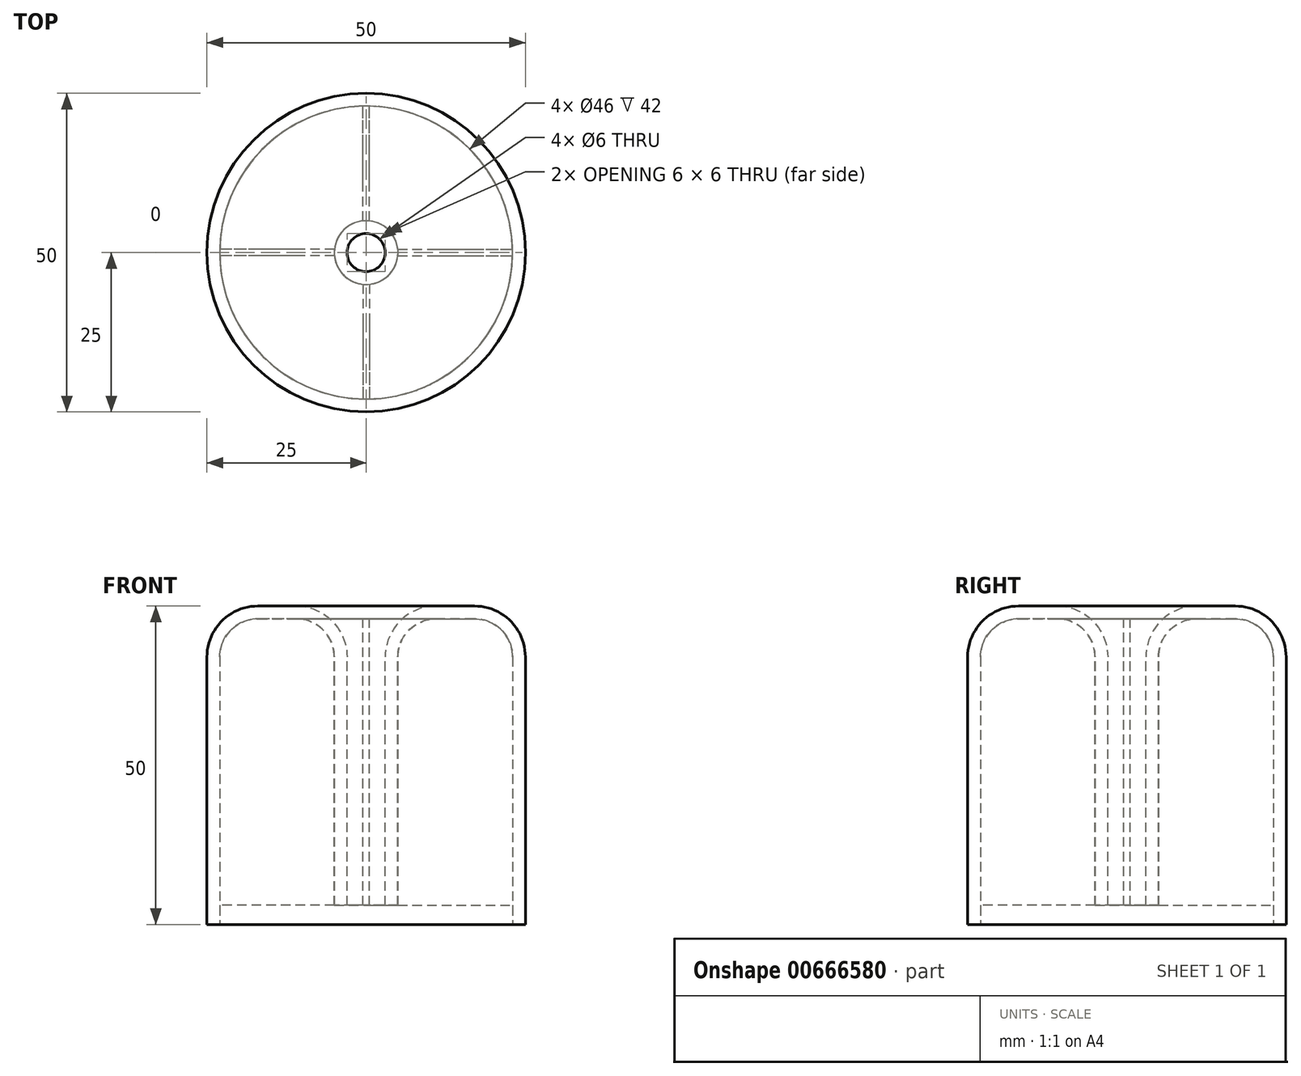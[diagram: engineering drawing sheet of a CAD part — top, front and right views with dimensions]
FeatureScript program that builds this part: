
annotation { "Feature Type Name" : "Feature", "Feature Type Description" : "" }
export const myFeature = defineFeature(function(context is Context, id is Id, definition is map)
    precondition{}
    {
        {
            var Q0;
            Q0=qCreatedBy(makeId("Top.planeOp"),FACE);
            var sketch = newSketch(context, id + "F0", { "sketchPlane" : qUnion([Q0])});
            skCircle(sketch, "E0", {"center": v(0, 0) * mm, "radius": 25 * mm});
            skSolve(sketch);
        }
        {
            var Q0;
            Q0 = qSketchRegion(id + "F0", true);
            extrude(context, id + "F1", {"entities" : qUnion([Q0]), "depth" : 50 * mm, "offsetDistance" : 25 * mm});
        }
        {
            var Q0;
            Q0=makeQuery(id+"F1.opExtrude","CAP_FACE",FACE,{"disambiguationData":[OSD([sQuery(id+"F0.wireOp",EDGE,"E0")])],"isStart":false});
            var sketch = newSketch(context, id + "F2", { "sketchPlane" : qUnion([Q0])});
            skCircle(sketch, "E1", {"center": v(0, 0) * mm, "radius": 3 * mm});
            skSolve(sketch);
        }
        {
            var Q0;
            Q0 = qSketchRegion(id + "F2", true);
            extrude(context, id + "F3", {"entities" : qUnion([Q0]), "operationType" : NewBodyOperationType.REMOVE, "oppositeDirection" : true, "depth" : 48 * mm, "offsetDistance" : 25 * mm});
        }
        {
            var Q0;
            Q0=makeQuery(id+"F1.opExtrude","CAP_FACE",FACE,{"disambiguationData":[OSD([sQuery(id+"F0.wireOp",EDGE,"E0")])],"isStart":false});
            fillet(context, id + "F4", {"entities" : qUnion([Q0]), "radius" : 8 * mm, "tangentPropagation" : true, "allowEdgeOverflow" : false});
        }
        {
            var Q0;
            Q0=makeQuery(id+"F1.opExtrude","CAP_FACE",FACE,{"disambiguationData":[OSD([sQuery(id+"F0.wireOp",EDGE,"E0")])],"isStart":true});
            shell(context, id + "F5", {"entities" : qUnion([Q0]), "thickness" : 2 * mm});
        }
        {
            var Q0;
            {var subQ0=sQuery(id+"F2.wireOp",EDGE,"E1");Q0=makeQuery(id+"F5.opShell","OFFSET_FACE",FACE,{"disambiguationData":[OSD([subQ0]),TDD([makeQuery(id+"F3.boolean.opBoolean","COPY",FACE,{"derivedFrom":makeQuery(id+"F3.opExtrude","CAP_FACE",FACE,{"disambiguationData":[OSD([subQ0])],"isStart":false})})])]});}
            var sketch = newSketch(context, id + "F6", { "sketchPlane" : qUnion([Q0])});
            skCircle(sketch, "E2.0", {"center": v(0, 0) * mm, "radius": 5 * mm});
            skSolve(sketch);
        }
        {
            var Q0;
            Q0 = qSketchRegion(id + "F6", true);
            extrude(context, id + "F7", {"entities" : qUnion([Q0]), "operationType" : NewBodyOperationType.REMOVE, "oppositeDirection" : true, "depth" : 3 * mm, "offsetDistance" : 25 * mm});
        }
        {
            var Q0;
            Q0=makeQuery(id+"F7.boolean.opBoolean","COPY",FACE,{"derivedFrom":makeQuery(id+"F7.opExtrude","CAP_FACE",FACE,{"disambiguationData":[OSD([sQuery(id+"F6.wireOp",EDGE,"E2.0")])],"isStart":false})});
            var sketch = newSketch(context, id + "F8", { "sketchPlane" : qUnion([Q0])});
            skLineSegment(sketch, "E3", {"start": v(0, 0) * mm, "end": v(0, -25.03) * mm, "construction": true});
            skLineSegment(sketch, "E4.0", {"start": v(-0.5, -3.8) * mm, "end": v(-0.5, -23.9) * mm});
            skLineSegment(sketch, "E5.0", {"start": v(0.5, -3.8) * mm, "end": v(0.5, -23.9) * mm});
            skLineSegment(sketch, "E6", {"start": v(0.5, -23.9) * mm, "end": v(-0.5, -23.9) * mm});
            skLineSegment(sketch, "E7", {"start": v(0.5, -3.8) * mm, "end": v(-0.5, -3.8) * mm});
            skSolve(sketch);
        }
        {
            var Q0;
            Q0 = qSketchRegion(id + "F8", true);
            extrude(context, id + "F9", {"entities" : qUnion([Q0]), "operationType" : NewBodyOperationType.ADD, "endBound" : BoundingType.UP_TO_NEXT, "oppositeDirection" : true, "depth" : 25 * mm, "offsetDistance" : 25 * mm});
        }
        {
            var Q0;
            Q0=makeQuery(id+"F1.opExtrude","SWEPT_BODY",BODY,{"disambiguationData":[OSD([sQuery(id+"F0.wireOp",EDGE,"E0")])]});
            var Q1;
            Q1=makeQuery(id+"F7.boolean.opBoolean","INTERSECT",EDGE,{"derivedFrom":[makeQuery(id+"F3.boolean.opBoolean","COPY",FACE,{"derivedFrom":makeQuery(id+"F3.opExtrude","SWEPT_FACE",FACE,{"disambiguationData":[OSD([sQuery(id+"F2.wireOp",EDGE,"E1")])]})}),makeQuery(id+"F7.opExtrude","CAP_FACE",FACE,{"disambiguationData":[OSD([sQuery(id+"F6.wireOp",EDGE,"E2.0")])],"isStart":false})]});
            circularPattern(context, id + "F10", {"entities" : qUnion([Q0]), "axis" : qUnion([Q1]), "angle" : 360 * degree, "instanceCount" : 4, "equalSpace" : true});
        }
    });
